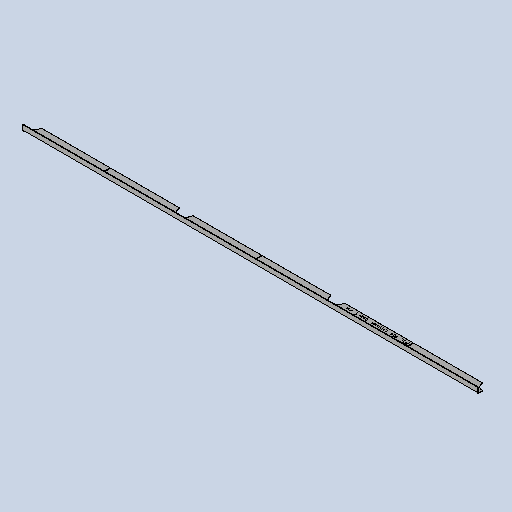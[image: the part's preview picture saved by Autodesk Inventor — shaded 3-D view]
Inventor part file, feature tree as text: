
AUTODESK INVENTOR PART (.ipt)
format: ipt  version: 2025 (Build 290162010, 162A)  size: 344,576 bytes
history: native  units: mm
features: sketch x6, other x5, sheet_metal_op x4, extrude x3, mirror x2, pattern_linear x1, projected_geometry x1
ambient origin geometry x8: Origin, YZ Plane, XZ Plane, XY Plane, X Axis, Y Axis, Z Axis, Center Point
bodies: Solid1 (feature_tree)
feature tree (22):
  sheet_metal_op  "Face1"
  sheet_metal_op  "Flange1"
  extrude  "Extrusion1"  Depth=39.0mm
  pattern_linear  "Rectangular Pattern1"  Count1=2 Spacing1=90.0deg
  extrude  "Extrusion2"  Depth=8.0mm
  mirror  "Mirror1"
  extrude  "Extrusion3"  Depth=2.0mm
  mirror  "Mirror2"
  other  "Mark1"
  other  "A-Side Definition"
  sketch  "Sketch1"  dims[d0=1500.0mm d1=39.0mm]
  other  "Plate1"
  sketch  "Sketch2"  dims[d2=2.0mm]
  other  "Plate2"
  sheet_metal_op  "Bend1"
  sheet_metal_op  "Corner1"
  sketch  "Sketch5"  dims[d3=2.0mm]
  sketch  "Sketch6"  dims[d4=1.0mm]
  sketch  "Sketch7"  dims[d5=4.0mm]
  projected_geometry  "Projected Loop3"
  sketch  "Sketch8"  dims[d6=2.75mm d7=20.0mm d8=90.0deg d9=2.75mm d10=8.0mm d11=2.0mm d12=2.75mm d15=0.0mm d16=0.0mm d18=2.0mm d21=30.0mm d23=500.0mm d24=45.0mm d25=30.0mm d26=0.0mm d27=2.0mm d28=20.0mm d29=100.0mm d30=10.0mm d31=10.0mm d32=20.0mm d33=0.0mm d34=0.0mm d35=200.0mm d36=12.0mm d39=5.0mm d40=5.0mm]
  other  "Definition1"
